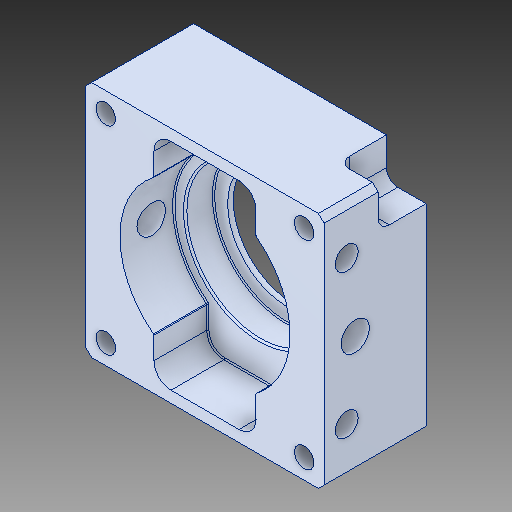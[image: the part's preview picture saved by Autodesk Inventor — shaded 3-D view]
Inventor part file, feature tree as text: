
AUTODESK INVENTOR PART (.ipt)
format: ipt  version: 2017 (Build 210142000, 142)  size: 295,424 bytes
history: native  units: in
note: dims shown in document units (in); Inventor stores cm internally (conversion verified against a paired STEP export)
features: hole x1
ambient origin geometry x8: Origin, YZ Plane, XZ Plane, XY Plane, X Axis, Y Axis, Z Axis, Center Point
bodies: Solid1 (feature_tree)
feature tree (1):
  hole  "Hole1"  [1 undecoded]
note: 1 required parameter value undecoded (feature->parameter linkage not recoverable at this tier; creation-order binding heuristic only, values carry confidence <= 0.55)
